# Revit family: Hager-Orion_Plus-IP65-D300-Cl.II-Poly_double_encl-630A-PT-pt
name_source: partatom
category: Electrical Equipment
units: mm (PartAtom-declared; Revit-internal decimal feet)

## family parameters
Cut with Voids When Loaded = No
Host = Face
Panel Configuration = Two Columns, Circuits Across
Part Type = Panelboard
Room Calculation Point = No
Round Connector Dimension = Use Diameter
Shared = No

## types (6) — shared parameters
EF000003 - Método de montagem = EV000384 - Montagem em superfície (gesso)
EF000007 - Cor = EV000270 - Cinzento
EF000049 - Profundidade = 300 mm  [stored 0.984252 ft]
EF000116 - Número RAL = 7035
EF000266 - Número de linhas = 3
EF001131 - Profundidade interior = 300 mm  [stored 0.984252 ft]
EF001596 - Material do corpo = EV000139 - Plástico
EF001613 - Integridade do circuito = EV000494 - Nenhum
EF004464 - Tipo de porta = EV002646 - Único
EF005474 - Grau de proteção (IP) = EV006421 - IP65
EF006306 - Com fecho = Yes
EF007800 - Adequado para proteção contra raios = No
EF008873 - Corrente nominal (In) = 630 A
EF009170 - Espessura do material do invólucro = 2 mm  [stored 0.00656168 ft]
EF009171 - Espessura do material da porta/tampa = 2 mm  [stored 0.00656168 ft]
EF015940 - Tampa com libertação de sobrepressão = No
HG000003 - Gama = Orion Plus
HG000006 - Encastrado = No
HG000010 - Portas assimétricas = No
HG000023 - Recinto de secção dupla = Yes
HG000024 - Altura da secção inferior = 800 mm  [stored 2.62467 ft]
HG000026 - Instalação no chão = No
HG000027 - Altura da Plinta = 70 mm  [stored 0.229659 ft]
Manufacturer = Hager
Type Comments = Orion Plus
zero-valued in all types: Default Elevation, EF000218 - Profundidade incorporada, EF000437 - Número de entradas de condutores, EF002950 - Largura em número de módulos, EF009554 - Número de aberturas para placas de flange

## per-type parameters (varying)
| type | EF000008 - Largura | EF000040 - Altura | EF000118 - Com tampa de montagem | EF000339 - Tipo de difusor | EF001088 - Extensão possível | EF003532 - Adequado para uso no exterior | EF004293 - Força de impacto | EF004427 - Número de módulos | EF006244 - Tampa/porta transparente | EF009212 - Tipo de tampa | HG000002 - Com porta ou tampa | HG000004 - Referência do Fabricante | HG000009 - Porta dupla |
| Montagem em superfície (gesso) IP65 L1100 A1150 P300  - FL360B | 1100 mm | 1150 mm | No | EV004216 - Porta | Yes | Yes | EV008784 - IK10 | 138 | Yes | EV009916 - Com recuo | Yes | FL360B | Yes |
| Montagem em superfície (gesso) IP65 L1100 A1450 P300  - FL362B | 1100 mm | 1450 mm | No | EV004216 - Porta | Yes | Yes | EV008784 - IK10 | 138 | Yes | EV009916 - Com recuo | Yes | FL362B | Yes |
| Montagem em superfície (gesso) IP65 L600 A1150 P300  - FL340B | 600 mm | 1150 mm | No | EV004216 - Porta | Yes | Yes | EV008784 - IK10 | 69 | Yes | EV009916 - Com recuo | Yes | FL340B | No |
| Montagem em superfície (gesso) IP65 L600 A1450 P300  - FL342B | 600 mm | 1450 mm | No | EV004216 - Porta | Yes | Yes | EV008784 - IK10 | 69 | Yes | EV009916 - Com recuo | No | FL342B | No |
| Montagem em superfície (gesso) IP65 L850 A1150 P300  - FL350B | 850 mm  [stored 2.78871 ft] | 1150 mm | No | EV004216 - Porta | Yes | Yes | EV008784 - IK10 | 111 | Yes | EV009916 - Com recuo | Yes | FL350B | No |
| Montagem em superfície (gesso) IP65 L850 A1450 P300  - FL352B | 850 mm  [stored 2.78871 ft] | 1450 mm | Yes | EV001012 - Tampa | No | No | EV006814 - IK08 | 111 | No | EV000116 - Fechado | Yes | FL352B | No |

note: [stored X ft] marks values corroborated as IEEE doubles in the binary element streams (Revit-internal decimal feet)

## geometry (parser evidence)
native form markers: Sweep x10
no freeform markers — native parametric forms only
